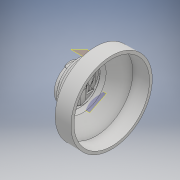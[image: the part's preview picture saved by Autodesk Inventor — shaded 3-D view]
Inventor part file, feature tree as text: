
AUTODESK INVENTOR PART (.ipt)
format: ipt  version: 2018 (Build 220112000, 112)  size: 2,399,744 bytes
history: native  units: mm
features: sketch x64, extrude x56, fillet x15, revolve x2, plane x2, mirror x1
ambient origin geometry x8: Origin, YZ Plane, XZ Plane, XY Plane, X Axis, Y Axis, Z Axis, Center Point
bodies: Solid1 (feature_tree)
feature tree (140):
  extrude  "Extrusion1"  TaperAngle=0.0deg  [1 undecoded]
  extrude  "Extrusion2"  Depth=10.0mm TaperAngle=0.0deg
  extrude  "Extrusion3"  Depth=50.0mm
  extrude  "Extrusion4"  TaperAngle=0.0deg  [1 undecoded]
  extrude  "Extrusion5"  Depth=10.0mm TaperAngle=0.0deg
  sketch  "Sketch6"  dims[d19=10.0mm d20=0.0mm d21=40.0mm]
  extrude  "Extrusion6"  Depth=40.0mm
  extrude  "Extrusion7"  Depth=11.0mm TaperAngle=0.0deg
  extrude  "Extrusion8"  Depth=32.0mm TaperAngle=0.0deg
  extrude  "Extrusion9"  Depth=32.0mm TaperAngle=0.0deg
  extrude  "Extrusion10"  Depth=10.0mm TaperAngle=0.0deg
  extrude  "Extrusion11"  Depth=10.0mm TaperAngle=0.0deg
  extrude  "Extrusion12"  TaperAngle=0.0deg  [1 undecoded]
  extrude  "Extrusion14"  Depth=48.3mm
  extrude  "Extrusion15"  TaperAngle=0.0deg  [1 undecoded]
  extrude  "Extrusion16"  Depth=10.0mm TaperAngle=0.0deg
  extrude  "Extrusion17"  Depth=11.63mm TaperAngle=0.0deg
  sketch  "Sketch21"  dims[d83=0.0mm d84=0.0mm d85=0.0mm d86=0.0mm]
  extrude  "Extrusion19"  Depth=11.63mm TaperAngle=0.0deg
  extrude  "Extrusion20"  TaperAngle=0.0deg  [1 undecoded]
  extrude  "Extrusion21"  Depth=10.0mm TaperAngle=0.0deg
  extrude  "Extrusion22"  TaperAngle=0.0deg  [1 undecoded]
  extrude  "Extrusion23"  Depth=2.86mm TaperAngle=0.0deg
  extrude  "Extrusion24"  Depth=2.01mm
  extrude  "Extrusion25"  Depth=10.0mm TaperAngle=0.0deg
  sketch  "Sketch33"  dims[d115=7.8mm d116=0.0mm d117=0.0mm d118=0.0mm]
  extrude  "Extrusion26"  Depth=7.8mm TaperAngle=0.0deg
  extrude  "Extrusion27"  TaperAngle=0.0deg  [1 undecoded]
  extrude  "Extrusion28"  Depth=22.0mm TaperAngle=0.0deg
  extrude  "Extrusion29"  Depth=17.0mm TaperAngle=0.0deg
  extrude  "Extrusion30"  Depth=2.0mm
  extrude  "Extrusion31"  Depth=6.95mm TaperAngle=0.0deg
  extrude  "Extrusion32"  Depth=18.0mm TaperAngle=0.0deg
  extrude  "Extrusion33"  Depth=1.02mm
  sketch  "Sketch42"  dims[d151=2.0mm d152=2.0mm]
  extrude  "Extrusion34"  Depth=7.72mm TaperAngle=0.0deg
  extrude  "Extrusion36"  Depth=2.0mm
  extrude  "Extrusion37"  Depth=2.0mm
  revolve  "Revolution3"  [1 undecoded]
  extrude  "Extrusion38"  Depth=2.0mm
  extrude  "Extrusion39"  Depth=10.0mm TaperAngle=0.0deg
  fillet  "Fillet1"  Radius=7.83mm
  fillet  "Fillet2"  Radius=20.0mm
  sketch  "Sketch51"
  extrude  "Extrusion41"  TaperAngle=90.0deg  [1 undecoded]
  mirror  "Mirror1"
  extrude  "Extrusion42"  Depth=1.15mm
  sketch  "Sketch54"
  sketch  "Sketch55"
  sketch  "Sketch56"
  extrude  "Extrusion44"  [1 undecoded]
  extrude  "Extrusion45"  [1 undecoded]
  extrude  "Extrusion46"  [1 undecoded]
  extrude  "Extrusion47"  [1 undecoded]
  plane  "Work Plane2"
  extrude  "Extrusion48"  [1 undecoded]
  extrude  "Extrusion49"  [1 undecoded]
  plane  "Work Plane5"
  extrude  "Extrusion50"  [1 undecoded]
  extrude  "Extrusion51"  [1 undecoded]
  fillet  "Fillet3"  [1 undecoded]
  fillet  "Fillet4"  [1 undecoded]
  extrude  "Extrusion52"  [1 undecoded]
  extrude  "Extrusion53"  [1 undecoded]
  extrude  "Extrusion54"  [1 undecoded]
  extrude  "Extrusion55"  [1 undecoded]
  fillet  "Fillet5"  [1 undecoded]
  extrude  "Extrusion57"  [1 undecoded]
  extrude  "Extrusion58"  [1 undecoded]
  extrude  "Extrusion59"  [1 undecoded]
  fillet  "Fillet7"  [1 undecoded]
  fillet  "Fillet8"  [1 undecoded]
  fillet  "Fillet9"  [1 undecoded]
  fillet  "Fillet10"  [1 undecoded]
  fillet  "Fillet11"  [1 undecoded]
  fillet  "Fillet12"  [1 undecoded]
  fillet  "Fillet13"  [1 undecoded]
  fillet  "Fillet14"  [1 undecoded]
  extrude  "Extrusion60"  [1 undecoded]
  extrude  "Extrusion61"  [1 undecoded]
  extrude  "Extrusion62"  [1 undecoded]
  sketch  "Sketch79"
  revolve  "Revolution4"  [1 undecoded]
  fillet  "Fillet15"  [1 undecoded]
  fillet  "Fillet16"  [1 undecoded]
  sketch  "Sketch1"  dims[d0=10.0mm d1=0.0mm d2=0.0mm d3=0.0mm]
  sketch  "Sketch2"  dims[d4=0.0mm d5=0.0mm d6=10.0mm d7=0.0mm]
  sketch  "Sketch3"  dims[d8=10.0mm d9=0.0mm d10=50.0mm]
  sketch  "Sketch4"  dims[d11=10.0mm d12=0.0mm d13=0.0mm d14=0.0mm]
  sketch  "Sketch5"  dims[d15=0.0mm d16=0.0mm d17=10.0mm d18=0.0mm]
  sketch  "Sketch7"  dims[d22=38.0mm d23=11.0mm d24=0.0mm]
  sketch  "Sketch8"  dims[d25=9.5mm d26=0.0mm d33=32.0mm d34=0.0mm]
  sketch  "Sketch9"  dims[d37=32.0mm d38=0.0mm d39=32.0mm d40=0.0mm]
  sketch  "Sketch10"  dims[d41=32.0mm d42=0.0mm d45=10.0mm d46=0.0mm]
  sketch  "Sketch11"  dims[d47=10.0mm d48=0.0mm d49=10.0mm d50=0.0mm]
  sketch  "Sketch12"  dims[d51=0.0mm d52=0.0mm d53=0.0mm d54=0.0mm]
  sketch  "Sketch13"  dims[d65=46.0mm d66=48.3mm]
  sketch  "Sketch16"  dims[d67=9.0mm d68=0.0mm d69=0.0mm d70=0.0mm]
  sketch  "Sketch18"  dims[d71=0.0mm d72=0.0mm d73=10.0mm d74=0.0mm]
  sketch  "Sketch19"  dims[d75=5.0mm d76=0.0mm d77=11.63mm d78=0.0mm]
  sketch  "Sketch20"  dims[d79=11.63mm d80=0.0mm d81=11.63mm d82=0.0mm]
  sketch  "Sketch22"  dims[d87=30.0mm d88=10.0mm d89=0.0mm]
  sketch  "Sketch23"  dims[d92=10.0mm d93=0.0mm d94=0.0mm d95=0.0mm]
  sketch  "Sketch24"  dims[d96=135.0deg d99=2.86mm d100=0.0mm]
  sketch  "Sketch25"  dims[d101=0.0mm d102=0.0mm d105=2.01mm]
  sketch  "Sketch31"  dims[d106=2.22mm d107=10.0mm d108=0.0mm]
  sketch  "Sketch32"  dims[d109=10.0mm d110=0.0mm d113=7.8mm d114=0.0mm]
  sketch  "Sketch34"  dims[d119=16.0mm d120=0.0mm d121=22.0mm d122=0.0mm]
  sketch  "Sketch35"  dims[d123=22.0mm d124=0.0mm d126=17.0mm d127=0.0mm]
  sketch  "Sketch36"  dims[d128=17.0mm d129=0.0mm d130=2.0mm]
  sketch  "Sketch37"  dims[d131=2.0mm d132=6.95mm d133=0.0mm]
  sketch  "Sketch38"  dims[d134=6.95mm d135=0.0mm d136=18.0mm d137=0.0mm]
  sketch  "Sketch39"  dims[d138=16.0mm d139=0.0mm d140=1.02mm]
  sketch  "Sketch40"  dims[d143=15.5mm d144=0.0mm d146=7.72mm d147=0.0mm]
  sketch  "Sketch41"  dims[d148=17.0mm d149=0.0mm d150=2.0mm]
  sketch  "Sketch43"  dims[d153=2.0mm d154=2.0mm]
  sketch  "Sketch45"  dims[d155=2.0mm d156=2.0mm]
  sketch  "Sketch47"  dims[d157=2.0mm d158=10.0mm d159=0.0mm d160=7.83mm d161=0.0mm d162=20.0mm d163=0.0mm]
  sketch  "Sketch48"  dims[d164=90.0deg d165=90.0deg]
  sketch  "Sketch49"  dims[d166=2.0mm d167=1.15mm]
  sketch  "Sketch52"
  sketch  "Sketch53"
  sketch  "Sketch57"
  sketch  "Sketch60"
  sketch  "Sketch61"
  sketch  "Sketch62"
  sketch  "Sketch63"
  sketch  "Sketch65"
  sketch  "Sketch66"
  sketch  "Sketch67"
  sketch  "Sketch68"
  sketch  "Sketch69"
  sketch  "Sketch70"
  sketch  "Sketch72"
  sketch  "Sketch73"
  sketch  "Sketch74"
  sketch  "Sketch75"
  sketch  "Sketch76"
  sketch  "Sketch78"
  sketch  "Sketch80"
note: 41 required parameter values undecoded (feature->parameter linkage not recoverable at this tier; creation-order binding heuristic only, values carry confidence <= 0.55)